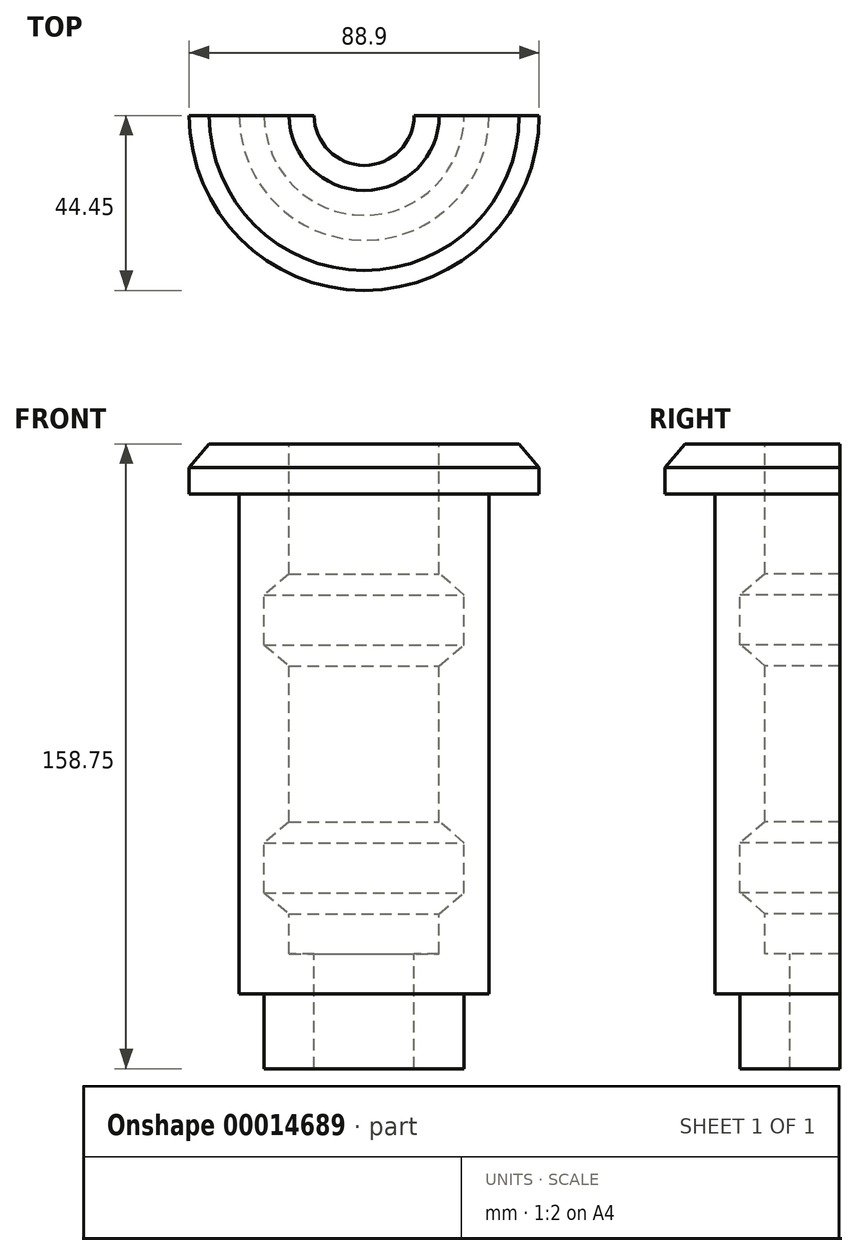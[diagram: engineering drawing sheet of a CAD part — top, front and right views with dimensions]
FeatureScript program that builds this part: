
annotation { "Feature Type Name" : "Feature", "Feature Type Description" : "" }
export const myFeature = defineFeature(function(context is Context, id is Id, definition is map)
    precondition{}
    {
        {
            var Q0;
            Q0=qCreatedBy(makeId("Front.planeOp"),FACE);
            var sketch = newSketch(context, id + "F0", { "sketchPlane" : qUnion([Q0])});
            skLineSegment(sketch, "E0", {"start": v(0, 103.37) * mm, "end": v(0, -114.86) * mm, "construction": true});
            skLineSegment(sketch, "E1", {"start": v(31.75, 63.5) * mm, "end": v(31.75, -63.5) * mm});
            skLineSegment(sketch, "E2", {"start": v(19.05, 106.24) * mm, "end": v(19.05, -152.57) * mm, "construction": true});
            skLineSegment(sketch, "E3", {"start": v(31.75, 63.5) * mm, "end": v(19.05, 63.5) * mm});
            skLineSegment(sketch, "E4", {"start": v(31.75, -63.5) * mm, "end": v(0, -63.5) * mm});
            skLineSegment(sketch, "E5", {"start": v(19.05, 63.5) * mm, "end": v(19.05, 43.18) * mm});
            skLineSegment(sketch, "E6", {"start": v(25.4, 132.18) * mm, "end": v(25.4, -143.64) * mm, "construction": true});
            skPoint(sketch, "E7", {"position": v(31.75, 0) * mm});
            skLineSegment(sketch, "E8", {"start": v(0, 0) * mm, "end": v(186.2, 0) * mm, "construction": true});
            skLineSegment(sketch, "E9", {"start": v(19.05, 43.18) * mm, "end": v(25.4, 37.85) * mm});
            skLineSegment(sketch, "E10", {"start": v(25.4, 37.85) * mm, "end": v(25.4, 25.15) * mm});
            skLineSegment(sketch, "E11", {"start": v(25.4, 25.15) * mm, "end": v(19.05, 19.82) * mm});
            skLineSegment(sketch, "E12", {"start": v(19.05, 19.82) * mm, "end": v(19.05, 0) * mm});
            skLineSegment(sketch, "E13.MirrorCS", {"start": v(19.05, -19.82) * mm, "end": v(19.05, 0) * mm});
            skLineSegment(sketch, "E14.MirrorCS", {"start": v(25.4, -25.15) * mm, "end": v(19.05, -19.82) * mm});
            skLineSegment(sketch, "E15.MirrorCS", {"start": v(25.4, -37.85) * mm, "end": v(25.4, -25.15) * mm});
            skLineSegment(sketch, "E16.MirrorCS", {"start": v(19.05, -43.18) * mm, "end": v(25.4, -37.85) * mm});
            skLineSegment(sketch, "E17.MirrorCS", {"start": v(19.05, -53.34) * mm, "end": v(19.05, -43.18) * mm});
            skLineSegment(sketch, "E18", {"start": v(19.05, -53.34) * mm, "end": v(12.7, -53.34) * mm});
            skPoint(sketch, "E18.endSnap0", {"position": v(19.05, -53.34) * mm});
            skLineSegment(sketch, "E19", {"start": v(12.7, -53.34) * mm, "end": v(12.7, -63.5) * mm});
            skPoint(sketch, "E20.orphan", {"position": v(19.05, -63.5) * mm});
            skLineSegment(sketch, "E21", {"start": v(31.75, 63.5) * mm, "end": v(50.03, 63.5) * mm});
            skLineSegment(sketch, "E22", {"start": v(50.03, 63.5) * mm, "end": v(39.37, 76.2) * mm});
            skLineSegment(sketch, "E23", {"start": v(39.37, 76.2) * mm, "end": v(19.05, 76.2) * mm});
            skLineSegment(sketch, "E24", {"start": v(19.05, 76.2) * mm, "end": v(19.05, 63.5) * mm});
            skLineSegment(sketch, "E25", {"start": v(12.7, -63.5) * mm, "end": v(12.7, -82.55) * mm});
            skLineSegment(sketch, "E26", {"start": v(12.7, -82.55) * mm, "end": v(25.4, -82.55) * mm});
            skLineSegment(sketch, "E27", {"start": v(25.4, -82.55) * mm, "end": v(25.4, -63.5) * mm});
            skPoint(sketch, "E28", {"position": v(25.4, 31.5) * mm});
            skPoint(sketch, "E29", {"position": v(25.4, -31.5) * mm});
            skSolve(sketch);
        }
        {
            var Q0;
            Q0=makeQuery(id+"F0.imprint","IMPRINT",FACE,{"disambiguationData":[TD([[makeQuery(id+"F0.imprint","IMPRINT",EDGE,{"derivedFrom":sQuery(id+"F0.wireOp",EDGE,"E3")}),-1.0]])]});
            var Q1;
            {var subQ3=sQuery(id+"F0.wireOp",EDGE,"E1");Q1=makeQuery(id+"F0.imprint","IMPRINT",FACE,{"disambiguationData":[TD([[makeQuery(id+"F0.imprint","IMPRINT",EDGE,{"derivedFrom":subQ3}),-1.0]])]});}
            var Q2;
            {var subQ1=sQuery(id+"F0.wireOp",EDGE,"E25");Q2=makeQuery(id+"F0.imprint","IMPRINT",FACE,{"disambiguationData":[TD([[makeQuery(id+"F0.imprint","IMPRINT",EDGE,{"derivedFrom":subQ1}),1.0]])]});}
            var Q3;
            Q3=sQuery(id+"F0.wireOp",EDGE,"E0");
            revolve(context, id + "F1", {"entities" : qUnion([Q0, Q1, Q2]), "axis" : qUnion([Q3]), "revolveType" : RevolveType.FULL});
        }
        {
            var Q0;
            Q0=makeQuery(id+"F1.opRevolve","SWEPT_FACE",FACE,{"disambiguationData":[OSD([sQuery(id+"F0.wireOp",EDGE,"E21")])]});
            var sketch = newSketch(context, id + "F2", { "sketchPlane" : qUnion([Q0])});
            skCircle(sketch, "E30", {"center": v(0, 0) * mm, "radius": 44.45 * mm});
            skCircle(sketch, "E31", {"center": v(0, 0) * mm, "radius": 63.5 * mm});
            skSolve(sketch);
        }
        {
            var Q0;
            Q0=makeQuery(id+"F2.imprint","IMPRINT",FACE,{"disambiguationData":[TD([[makeQuery(id+"F2.imprint","IMPRINT",EDGE,{"derivedFrom":sQuery(id+"F2.wireOp",EDGE,"E30")}),-1.0]])]});
            extrude(context, id + "F3", {"entities" : qUnion([Q0]), "operationType" : NewBodyOperationType.REMOVE, "endBound" : BoundingType.THROUGH_ALL, "oppositeDirection" : true, "depth" : 25.4 * mm});
        }
        {
            var Q0;
            Q0=qCreatedBy(makeId("Front.planeOp"),FACE);
            var sketch = newSketch(context, id + "F4", { "sketchPlane" : qUnion([Q0])});
            skLineSegment(sketch, "E32.bottom", {"start": v(165.4, 215.37) * mm, "end": v(-123.7, 215.37) * mm});
            skLineSegment(sketch, "E32.top", {"start": v(165.4, -250.97) * mm, "end": v(-123.7, -250.97) * mm});
            skLineSegment(sketch, "E32.left", {"start": v(165.4, 215.37) * mm, "end": v(165.4, -250.97) * mm});
            skLineSegment(sketch, "E32.right", {"start": v(-123.7, 215.37) * mm, "end": v(-123.7, -250.97) * mm});
            skSolve(sketch);
        }
        {
            var Q0;
            Q0=makeQuery(id+"F4.imprint","IMPRINT",FACE,{"disambiguationData":[TD([[makeQuery(id+"F4.imprint","IMPRINT",EDGE,{"derivedFrom":sQuery(id+"F4.wireOp",EDGE,"E32.bottom")}),1.0]])]});
            extrude(context, id + "F5", {"entities" : qUnion([Q0]), "operationType" : NewBodyOperationType.REMOVE, "endBound" : BoundingType.THROUGH_ALL, "oppositeDirection" : true, "depth" : 25 * mm});
        }
    });
